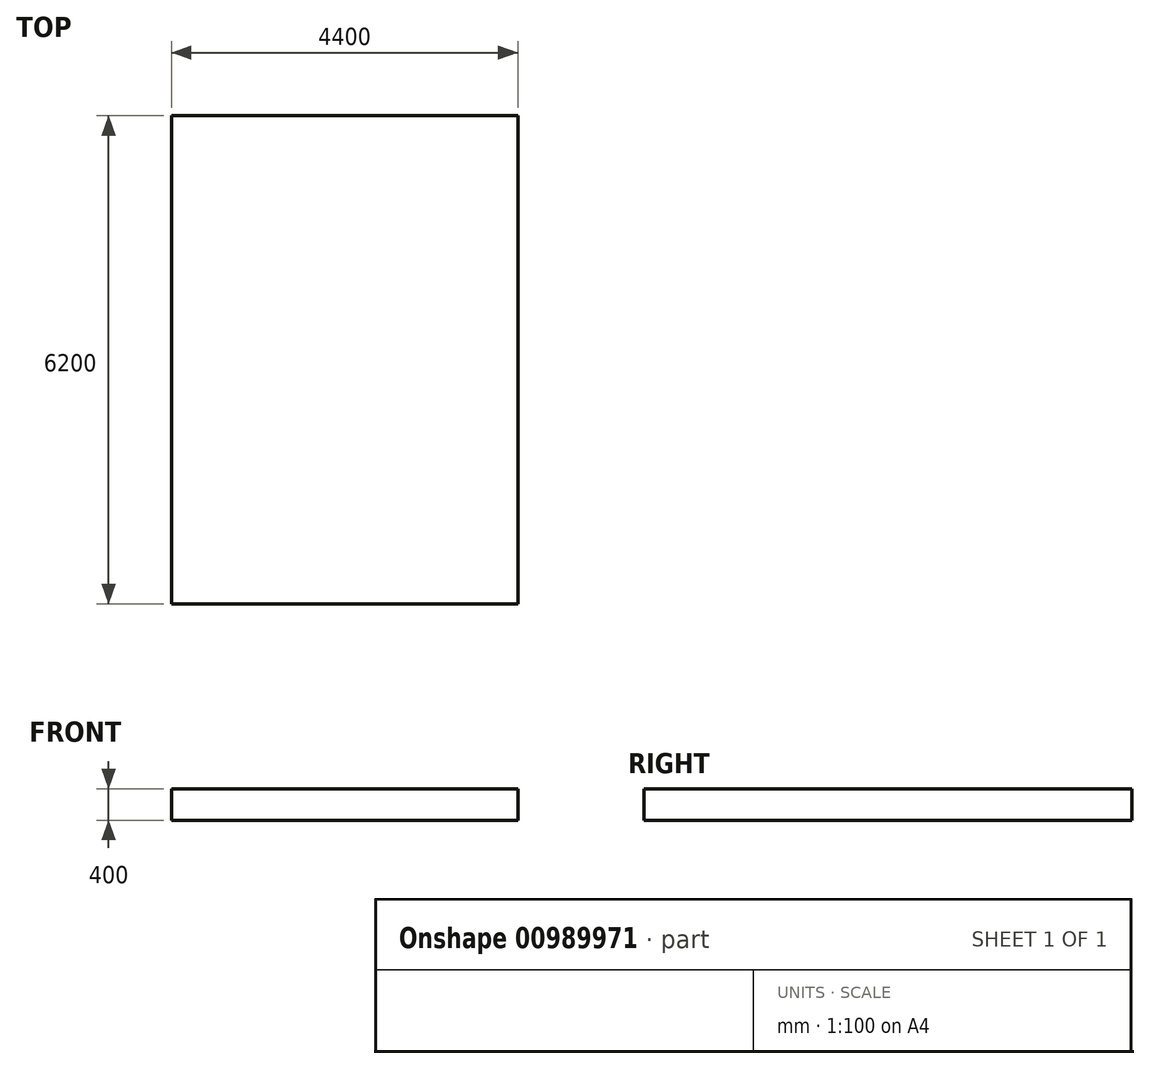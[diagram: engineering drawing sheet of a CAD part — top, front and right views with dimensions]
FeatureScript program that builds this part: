
annotation { "Feature Type Name" : "Feature", "Feature Type Description" : "" }
export const myFeature = defineFeature(function(context is Context, id is Id, definition is map)
    precondition{}
    {
        {
            var Q0;
            Q0=qCreatedBy(makeId("Top.planeOp"),FACE);
            var sketch = newSketch(context, id + "F0", { "sketchPlane" : qUnion([Q0])});
            skLineSegment(sketch, "E0.bottom", {"start": v(0, 0) * mm, "end": v(4400, 0) * mm});
            skLineSegment(sketch, "E0.top", {"start": v(0, -6200) * mm, "end": v(4400, -6200) * mm});
            skLineSegment(sketch, "E0.left", {"start": v(0, 0) * mm, "end": v(0, -6200) * mm});
            skLineSegment(sketch, "E0.right", {"start": v(4400, 0) * mm, "end": v(4400, -6200) * mm});
            skSolve(sketch);
        }
        {
            var Q0;
            Q0 = qSketchRegion(id + "F0", true);
            extrude(context, id + "F1", {"entities" : qUnion([Q0]), "depth" : -400 * mm, "offsetDistance" : 25 * mm});
        }
    });
